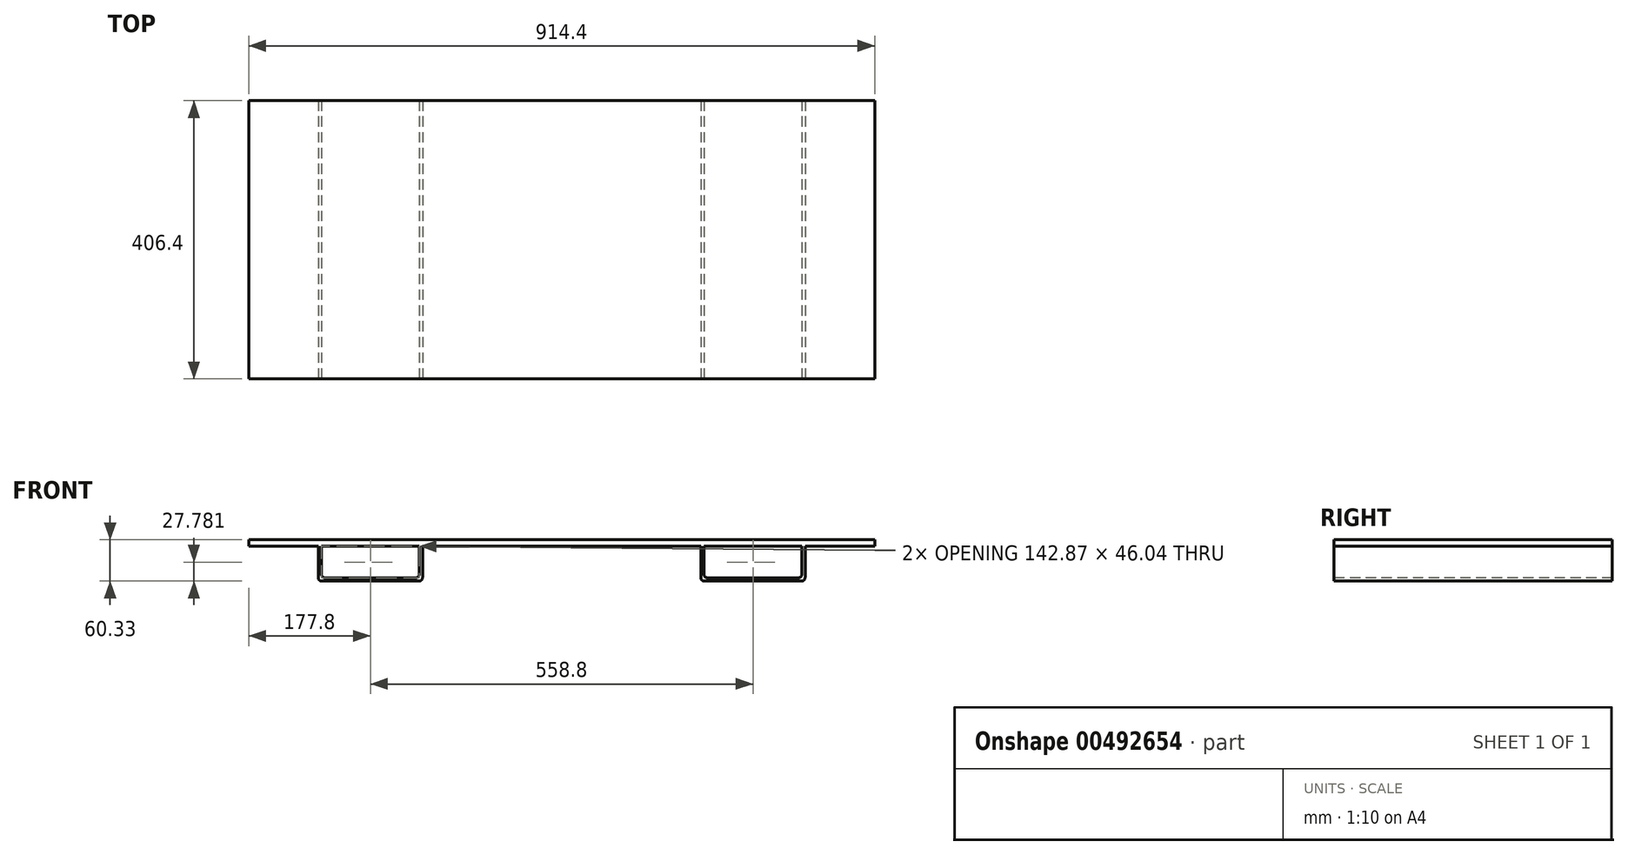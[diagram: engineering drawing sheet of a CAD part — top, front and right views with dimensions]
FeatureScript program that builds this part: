
annotation { "Feature Type Name" : "Feature", "Feature Type Description" : "" }
export const myFeature = defineFeature(function(context is Context, id is Id, definition is map)
    precondition{}
    {
        {
            var Q0;
            Q0=qCreatedBy(makeId("Top.planeOp"),FACE);
            var sketch = newSketch(context, id + "F0", { "sketchPlane" : qUnion([Q0])});
            skLineSegment(sketch, "E0.bottom", {"start": v(457.2, -203.2) * mm, "end": v(-457.2, -203.2) * mm});
            skLineSegment(sketch, "E0.top", {"start": v(457.2, 203.2) * mm, "end": v(-457.2, 203.2) * mm});
            skLineSegment(sketch, "E0.left", {"start": v(457.2, -203.2) * mm, "end": v(457.2, 203.2) * mm});
            skLineSegment(sketch, "E0.right", {"start": v(-457.2, -203.2) * mm, "end": v(-457.2, 203.2) * mm});
            skPoint(sketch, "E0.middle", {"position": v(0, 0) * mm});
            skSolve(sketch);
        }
        {
            var Q0;
            Q0 = qSketchRegion(id + "F0", true);
            extrude(context, id + "F1", {"entities" : qUnion([Q0]), "depth" : 9.52 * mm, "offsetDistance" : 25 * mm});
        }
        {
            var Q0;
            Q0=makeQuery(id+"F1.opExtrude","SWEPT_FACE",FACE,{"disambiguationData":[OSD([sQuery(id+"F0.wireOp",EDGE,"E0.bottom")])]});
            var sketch = newSketch(context, id + "F2", { "sketchPlane" : qUnion([Q0])});
            skLineSegment(sketch, "E1.bottom", {"start": v(-355.6, 0) * mm, "end": v(-203.2, 0) * mm});
            skLineSegment(sketch, "E1.top", {"start": v(-350.6, -50.8) * mm, "end": v(-208.2, -50.8) * mm});
            skLineSegment(sketch, "E1.left", {"start": v(-355.6, 0) * mm, "end": v(-355.6, -45.8) * mm});
            skLineSegment(sketch, "E1.right", {"start": v(-203.2, 0) * mm, "end": v(-203.2, -45.8) * mm});
            skLineSegment(sketch, "E2.bottom", {"start": v(-350.84, 0) * mm, "end": v(-207.96, 0) * mm});
            skLineSegment(sketch, "E2.top", {"start": v(-345.84, -46.04) * mm, "end": v(-212.96, -46.04) * mm});
            skLineSegment(sketch, "E2.left", {"start": v(-350.84, 0) * mm, "end": v(-350.84, -41.04) * mm});
            skLineSegment(sketch, "E2.right", {"start": v(-207.96, 0) * mm, "end": v(-207.96, -41.04) * mm});
            skLineSegment(sketch, "E3", {"start": v(-279.4, -50.8) * mm, "end": v(-279.4, 0) * mm, "construction": true});
            skLineSegment(sketch, "E4", {"start": v(0, 0) * mm, "end": v(0, -46.6) * mm, "construction": true});
            skLineSegment(sketch, "E5.MirrorCS", {"start": v(203.2, 0) * mm, "end": v(203.2, -45.8) * mm});
            skLineSegment(sketch, "E6.MirrorCS", {"start": v(207.96, 0) * mm, "end": v(207.96, -41.04) * mm});
            skLineSegment(sketch, "E7.MirrorCS", {"start": v(350.84, 0) * mm, "end": v(350.84, -41.04) * mm});
            skLineSegment(sketch, "E8.MirrorCS", {"start": v(355.6, 0) * mm, "end": v(355.6, -50.8) * mm});
            skLineSegment(sketch, "E9.MirrorCS", {"start": v(345.84, -46.04) * mm, "end": v(212.96, -46.04) * mm});
            skLineSegment(sketch, "E10.MirrorCS", {"start": v(355.6, -50.8) * mm, "end": v(208.2, -50.8) * mm});
            skLineSegment(sketch, "E11.MirrorCS", {"start": v(350.84, 0) * mm, "end": v(207.96, 0) * mm});
            skPoint(sketch, "E12.visualSharp", {"position": v(-355.6, -50.8) * mm});
            skArc(sketch, "E12.filletArc", {"start": v(-355.6, -45.8) * mm, "mid": v(-354.14, -49.34) * mm, "end": v(-350.6, -50.8) * mm});
            skPoint(sketch, "E13.visualSharp", {"position": v(-350.84, -46.04) * mm});
            skArc(sketch, "E13.filletArc", {"start": v(-350.84, -41.04) * mm, "mid": v(-349.37, -44.57) * mm, "end": v(-345.84, -46.04) * mm});
            skPoint(sketch, "E14.visualSharp", {"position": v(-207.96, -46.04) * mm});
            skArc(sketch, "E14.filletArc", {"start": v(-212.96, -46.04) * mm, "mid": v(-209.43, -44.57) * mm, "end": v(-207.96, -41.04) * mm});
            skPoint(sketch, "E15.visualSharp", {"position": v(-203.2, -50.8) * mm});
            skArc(sketch, "E15.filletArc", {"start": v(-208.2, -50.8) * mm, "mid": v(-204.66, -49.34) * mm, "end": v(-203.2, -45.8) * mm});
            skPoint(sketch, "E16.visualSharp", {"position": v(207.96, -46.04) * mm});
            skArc(sketch, "E16.filletArc", {"start": v(207.96, -41.04) * mm, "mid": v(209.43, -44.57) * mm, "end": v(212.96, -46.04) * mm});
            skPoint(sketch, "E17.visualSharp", {"position": v(203.2, -50.8) * mm});
            skArc(sketch, "E17.filletArc", {"start": v(203.2, -45.8) * mm, "mid": v(204.66, -49.34) * mm, "end": v(208.2, -50.8) * mm});
            skPoint(sketch, "E18.visualSharp", {"position": v(350.84, -46.04) * mm});
            skArc(sketch, "E18.filletArc", {"start": v(345.84, -46.04) * mm, "mid": v(349.37, -44.57) * mm, "end": v(350.84, -41.04) * mm});
            skSolve(sketch);
        }
        {
            var Q0;
            Q0=makeQuery(id+"F2.imprint","IMPRINT",FACE,{"disambiguationData":[TD([[makeQuery(id+"F2.imprint","IMPRINT",EDGE,{"derivedFrom":sQuery(id+"F2.wireOp",EDGE,"E1.top")}),1.0]])]});
            var Q1;
            {var subQ4=sQuery(id+"F2.wireOp",EDGE,"E5.MirrorCS");Q1=makeQuery(id+"F2.imprint","IMPRINT",FACE,{"disambiguationData":[TD([[makeQuery(id+"F2.imprint","IMPRINT",EDGE,{"derivedFrom":subQ4}),1.0]])]});}
            var Q2;
            Q2=makeQuery(id+"F1.opExtrude","SWEPT_FACE",FACE,{"disambiguationData":[OSD([sQuery(id+"F0.wireOp",EDGE,"E0.top")])]});
            extrude(context, id + "F3", {"entities" : qUnion([Q0, Q1]), "operationType" : NewBodyOperationType.ADD, "endBound" : BoundingType.UP_TO_SURFACE, "oppositeDirection" : true, "depth" : 25 * mm, "endBoundEntityFace" : qUnion([Q2]), "offsetDistance" : 25 * mm});
        }
        {
            var Q0;
            Q0=makeQuery(id+"F3.opExtrude","SWEPT_EDGE",EDGE,{"disambiguationData":[OSD([sQuery(id+"F2.wireOp",EDGE,"E8.MirrorCS"),sQuery(id+"F2.wireOp",EDGE,"E10.MirrorCS")])]});
            fillet(context, id + "F4", {"entities" : qUnion([Q0]), "radius" : 5 * mm, "tangentPropagation" : true, "allowEdgeOverflow" : false});
        }
    });
